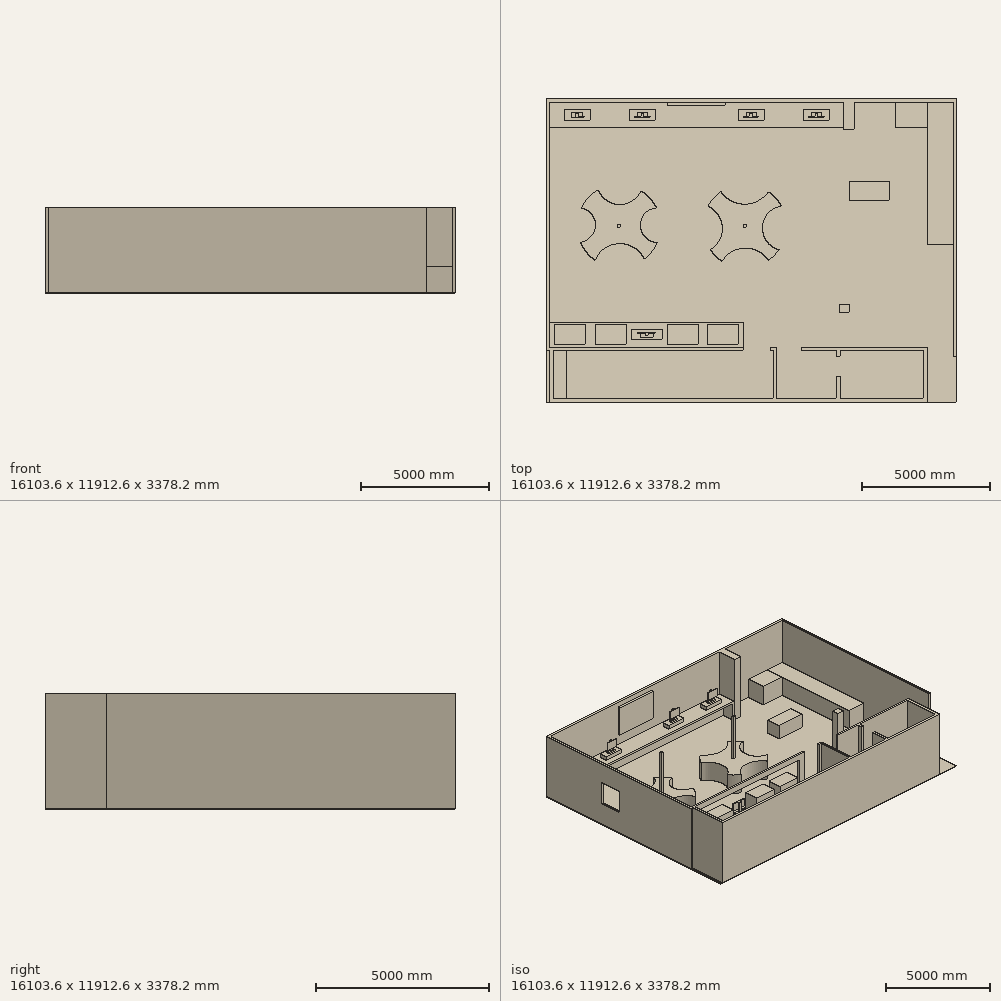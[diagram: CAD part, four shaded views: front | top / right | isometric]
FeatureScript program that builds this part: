
annotation { "Feature Type Name" : "Feature", "Feature Type Description" : "" }
export const myFeature = defineFeature(function(context is Context, id is Id, definition is map)
    precondition{}
    {
        {
            var Q0;
            Q0=qCreatedBy(makeId("Top.planeOp"),FACE);
            var sketch = newSketch(context, id + "F0", { "sketchPlane" : qUnion([Q0])});
            skLineSegment(sketch, "E0", {"start": v(0, 0) * mm, "end": v(0, 4876.8) * mm});
            skLineSegment(sketch, "E1", {"start": v(14833.6, -4876.8) * mm, "end": v(14833.6, -5130.8) * mm});
            skLineSegment(sketch, "E2", {"start": v(15849.6, -5130.8) * mm, "end": v(15849.6, 4876.8) * mm});
            skLineSegment(sketch, "E3", {"start": v(15849.6, 4876.8) * mm, "end": v(11963.4, 4876.8) * mm});
            skLineSegment(sketch, "E4", {"start": v(11963.4, 4876.8) * mm, "end": v(11963.4, 3810) * mm});
            skLineSegment(sketch, "E5", {"start": v(11963.4, 3810) * mm, "end": v(11557, 3810) * mm});
            skLineSegment(sketch, "E6", {"start": v(11557, 3810) * mm, "end": v(11557, 4876.8) * mm});
            skLineSegment(sketch, "E7", {"start": v(11760.2, 1757.31) * mm, "end": v(13335, 1757.31) * mm});
            skPoint(sketch, "E7.startSnap0", {"position": v(11760.2, 3810) * mm});
            skLineSegment(sketch, "E8", {"start": v(13335, 1757.31) * mm, "end": v(13335, 995.31) * mm});
            skLineSegment(sketch, "E9", {"start": v(13335, 995.31) * mm, "end": v(11760.2, 995.31) * mm});
            skLineSegment(sketch, "E10", {"start": v(11760.2, 995.31) * mm, "end": v(11760.2, 1757.31) * mm});
            skLineSegment(sketch, "E11", {"start": v(11760.2, -3062.9) * mm, "end": v(11379.2, -3062.9) * mm});
            skLineSegment(sketch, "E12", {"start": v(11379.2, -3062.9) * mm, "end": v(11379.2, -3393.1) * mm});
            skLineSegment(sketch, "E13", {"start": v(11379.2, -3393.1) * mm, "end": v(11760.2, -3393.1) * mm});
            skLineSegment(sketch, "E14", {"start": v(11760.2, -3393.1) * mm, "end": v(11760.2, -3062.9) * mm});
            skLineSegment(sketch, "E15", {"start": v(0, -4876.8) * mm, "end": v(0, -6908.8) * mm});
            skLineSegment(sketch, "E16", {"start": v(0, -6908.8) * mm, "end": v(8890, -6908.8) * mm});
            skLineSegment(sketch, "E17", {"start": v(8890, -6908.8) * mm, "end": v(14833.6, -6908.8) * mm});
            skLineSegment(sketch, "E18", {"start": v(14833.6, -6908.8) * mm, "end": v(14833.6, -5130.8) * mm});
            skLineSegment(sketch, "E19", {"start": v(11282.33, -4876.8) * mm, "end": v(11282.33, -5130.8) * mm});
            skLineSegment(sketch, "E20", {"start": v(2540, -4876.8) * mm, "end": v(7620, -4876.8) * mm});
            skLineSegment(sketch, "E21", {"start": v(15849.6, -5130.8) * mm, "end": v(15976.6, -5130.8) * mm});
            skLineSegment(sketch, "E22", {"start": v(15976.6, -5130.8) * mm, "end": v(15976.6, 5003.8) * mm});
            skLineSegment(sketch, "E23", {"start": v(15976.6, 5003.8) * mm, "end": v(-127, 5003.8) * mm});
            skLineSegment(sketch, "E24", {"start": v(-127, 5003.8) * mm, "end": v(-127, -4876.8) * mm});
            skLineSegment(sketch, "E25", {"start": v(-127, -4876.8) * mm, "end": v(0, -4876.8) * mm});
            skLineSegment(sketch, "E26", {"start": v(0, 0) * mm, "end": v(0, -4749.8) * mm});
            skLineSegment(sketch, "E27", {"start": v(0, -4749.8) * mm, "end": v(1524, -4749.8) * mm});
            skLineSegment(sketch, "E28", {"start": v(2540, -4749.8) * mm, "end": v(7620, -4749.8) * mm});
            skLineSegment(sketch, "E29", {"start": v(8662.75, -4876.8) * mm, "end": v(8662.75, -4749.8) * mm});
            skLineSegment(sketch, "E30", {"start": v(8662.75, -4749.8) * mm, "end": v(8890, -4749.8) * mm});
            skLineSegment(sketch, "E31", {"start": v(8890, -4749.8) * mm, "end": v(8890, -4876.8) * mm});
            skLineSegment(sketch, "E32", {"start": v(0, 4876.8) * mm, "end": v(11557, 4876.8) * mm});
            skLineSegment(sketch, "E33", {"start": v(8662.75, -4876.8) * mm, "end": v(8789.75, -4876.8) * mm});
            skLineSegment(sketch, "E34", {"start": v(8789.75, -4876.8) * mm, "end": v(8789.75, -6781.8) * mm});
            skLineSegment(sketch, "E35", {"start": v(8789.75, -6781.8) * mm, "end": v(153.75, -6781.8) * mm});
            skLineSegment(sketch, "E36", {"start": v(153.75, -6781.8) * mm, "end": v(153.75, -4876.8) * mm});
            skLineSegment(sketch, "E37", {"start": v(1524, -4876.8) * mm, "end": v(153.75, -4876.8) * mm});
            skLineSegment(sketch, "E38", {"start": v(7620, -4876.8) * mm, "end": v(7620, -4749.8) * mm});
            skLineSegment(sketch, "E39", {"start": v(9906, -4876.8) * mm, "end": v(9906, -4749.8) * mm});
            skLineSegment(sketch, "E40", {"start": v(9906, -4749.8) * mm, "end": v(14833.6, -4749.8) * mm});
            skLineSegment(sketch, "E41", {"start": v(14833.6, -4749.8) * mm, "end": v(14833.6, -4876.8) * mm});
            skLineSegment(sketch, "E42", {"start": v(11282.33, -5130.8) * mm, "end": v(11409.33, -5130.8) * mm});
            skLineSegment(sketch, "E43", {"start": v(11409.33, -5130.8) * mm, "end": v(11409.33, -4876.8) * mm});
            skLineSegment(sketch, "E44", {"start": v(11282.33, -5892.8) * mm, "end": v(11409.33, -5892.8) * mm});
            skLineSegment(sketch, "E45", {"start": v(11409.33, -5892.8) * mm, "end": v(11409.33, -6781.8) * mm});
            skLineSegment(sketch, "E46", {"start": v(9906, -4876.8) * mm, "end": v(11282.33, -4876.8) * mm});
            skLineSegment(sketch, "E47", {"start": v(11409.33, -4876.8) * mm, "end": v(14685.93, -4876.8) * mm});
            skLineSegment(sketch, "E48", {"start": v(14685.93, -4876.8) * mm, "end": v(14685.93, -6781.8) * mm});
            skLineSegment(sketch, "E49", {"start": v(14685.93, -6781.8) * mm, "end": v(11409.33, -6781.8) * mm});
            skLineSegment(sketch, "E50", {"start": v(8890, -4876.8) * mm, "end": v(8890, -6781.8) * mm});
            skLineSegment(sketch, "E51", {"start": v(8890, -6781.8) * mm, "end": v(11282.32, -6781.8) * mm});
            skLineSegment(sketch, "E52", {"start": v(11282.32, -6781.8) * mm, "end": v(11282.33, -5892.8) * mm});
            skLineSegment(sketch, "E53", {"start": v(1524, -4749.8) * mm, "end": v(2540, -4749.8) * mm});
            skLineSegment(sketch, "E54", {"start": v(1524, -4876.8) * mm, "end": v(2540, -4876.8) * mm});
            skSolve(sketch);
        }
        {
            var Q0;
            Q0=makeQuery(id+"F0.imprint","IMPRINT",FACE,{"disambiguationData":[TD([[makeQuery(id+"F0.imprint","IMPRINT",EDGE,{"derivedFrom":sQuery(id+"F0.wireOp",EDGE,"E0")}),1.0]])]});
            var Q1;
            Q1=makeQuery(id+"F0.imprint","IMPRINT",FACE,{"disambiguationData":[TD([[makeQuery(id+"F0.imprint","IMPRINT",EDGE,{"derivedFrom":sQuery(id+"F0.wireOp",EDGE,"E20")}),1.0]])]});
            var Q2;
            Q2=makeQuery(id+"F0.imprint","IMPRINT",FACE,{"disambiguationData":[TD([[makeQuery(id+"F0.imprint","IMPRINT",EDGE,{"derivedFrom":sQuery(id+"F0.wireOp",EDGE,"E11")}),1.0]])]});
            extrude(context, id + "F1", {"entities" : qUnion([Q0, Q1, Q2]), "depth" : 3352.8 * mm, "offsetDistance" : 25.4 * mm});
        }
        {
            var Q0;
            Q0=makeQuery(id+"F0.imprint","IMPRINT",FACE,{"disambiguationData":[TD([[makeQuery(id+"F0.imprint","IMPRINT",EDGE,{"derivedFrom":sQuery(id+"F0.wireOp",EDGE,"E7")}),-1.0]])]});
            extrude(context, id + "F2", {"entities" : qUnion([Q0]), "depth" : 736.6 * mm, "offsetDistance" : 25.4 * mm});
        }
        {
            var Q0;
            Q0=makeQuery(id+"F0.imprint","IMPRINT",FACE,{"disambiguationData":[TD([[makeQuery(id+"F0.imprint","IMPRINT",EDGE,{"derivedFrom":sQuery(id+"F0.wireOp",EDGE,"E0")}),1.0]])]});
            var sketch = newSketch(context, id + "F3", { "sketchPlane" : qUnion([Q0])});
            skLineSegment(sketch, "E55.0", {"start": v(-127, 5003.8) * mm, "end": v(-127, -4876.8) * mm});
            skLineSegment(sketch, "E56.0", {"start": v(0, -6908.8) * mm, "end": v(8890, -6908.8) * mm});
            skLineSegment(sketch, "E57.0", {"start": v(15976.6, 5003.8) * mm, "end": v(-127, 5003.8) * mm});
            skLineSegment(sketch, "E58.0", {"start": v(15976.6, -5130.8) * mm, "end": v(15976.6, 5003.8) * mm});
            skLineSegment(sketch, "E59.bottom", {"start": v(-127, -6908.8) * mm, "end": v(15976.6, -6908.8) * mm});
            skLineSegment(sketch, "E59.top", {"start": v(-127, 5003.8) * mm, "end": v(15976.6, 5003.8) * mm});
            skLineSegment(sketch, "E59.left", {"start": v(-127, -6908.8) * mm, "end": v(-127, 5003.8) * mm});
            skLineSegment(sketch, "E59.right", {"start": v(15976.6, -6908.8) * mm, "end": v(15976.6, 5003.8) * mm});
            skSolve(sketch);
        }
        {
            var Q0;
            Q0 = qSketchRegion(id + "F3", true);
            extrude(context, id + "F4", {"entities" : qUnion([Q0]), "oppositeDirection" : true, "depth" : 25.4 * mm, "offsetDistance" : 25.4 * mm});
        }
        {
            var Q0;
            Q0=makeQuery(id+"F1.opExtrude","SWEPT_FACE",FACE,{"disambiguationData":[OSD([sQuery(id+"F0.wireOp",EDGE,"E0"),sQuery(id+"F0.wireOp",EDGE,"E26")])]});
            var sketch = newSketch(context, id + "F5", { "sketchPlane" : qUnion([Q0])});
            skLineSegment(sketch, "E60", {"start": v(0, 1143) * mm, "end": v(1231.9, 1143) * mm});
            skLineSegment(sketch, "E61", {"start": v(1231.9, 1143) * mm, "end": v(1231.9, 2311.4) * mm});
            skLineSegment(sketch, "E62", {"start": v(1231.9, 2311.4) * mm, "end": v(0, 2311.4) * mm});
            skLineSegment(sketch, "E63", {"start": v(0, 2311.4) * mm, "end": v(0, 1143) * mm});
            skSolve(sketch);
        }
        {
            var Q0;
            Q0 = qSketchRegion(id + "F5", true);
            extrude(context, id + "F6", {"entities" : qUnion([Q0]), "operationType" : NewBodyOperationType.REMOVE, "oppositeDirection" : true, "depth" : 177.8 * mm, "offsetDistance" : 25.4 * mm});
        }
        {
            var Q0;
            Q0=makeQuery(id+"F4.opExtrude","CAP_FACE",FACE,{"disambiguationData":[OSD([sQuery(id+"F3.wireOp",EDGE,"E59.bottom"),sQuery(id+"F3.wireOp",EDGE,"E59.top"),sQuery(id+"F3.wireOp",EDGE,"E59.left"),sQuery(id+"F3.wireOp",EDGE,"E59.right")])],"isStart":true});
            var sketch = newSketch(context, id + "F7", { "sketchPlane" : qUnion([Q0])});
            skCircle(sketch, "E64", {"center": v(2722.99, 0) * mm, "radius": 1638.3 * mm});
            skCircle(sketch, "E65", {"center": v(7663.59, 0) * mm, "radius": 1640.13 * mm});
            skSolve(sketch);
        }
        {
            var Q0;
            Q0=makeQuery(id+"F7.imprint","IMPRINT",FACE,{"disambiguationData":[TD([[makeQuery(id+"F7.imprint","IMPRINT",EDGE,{"derivedFrom":sQuery(id+"F7.wireOp",EDGE,"E64")}),1.0]])]});
            var Q1;
            Q1=makeQuery(id+"F7.imprint","IMPRINT",FACE,{"disambiguationData":[TD([[makeQuery(id+"F7.imprint","IMPRINT",EDGE,{"derivedFrom":sQuery(id+"F7.wireOp",EDGE,"E65")}),1.0]])]});
            extrude(context, id + "F8", {"entities" : qUnion([Q0, Q1]), "operationType" : NewBodyOperationType.ADD, "depth" : 1016 * mm, "offsetDistance" : 25.4 * mm});
        }
        {
            var Q0;
            Q0=makeQuery(id+"F8.opExtrude","CAP_FACE",FACE,{"disambiguationData":[OSD([sQuery(id+"F7.wireOp",EDGE,"E64")])],"isStart":false});
            var sketch = newSketch(context, id + "F9", { "sketchPlane" : qUnion([Q0])});
            skArc(sketch, "E66", {"start": v(1906.26, 1420.2) * mm, "mid": v(2740.7, 849.85) * mm, "end": v(3598.19, 1384.94) * mm});
            skArc(sketch, "E67", {"start": v(1213.38, -636.47) * mm, "mid": v(1800.18, 23.44) * mm, "end": v(1247.63, 712.29) * mm});
            skArc(sketch, "E68", {"start": v(3721.77, -1298.64) * mm, "mid": v(2740.3, -685.3) * mm, "end": v(1791.02, -1347.4) * mm});
            skArc(sketch, "E69", {"start": v(4198.34, 712.29) * mm, "mid": v(3564.92, 21.38) * mm, "end": v(4232.6, -636.47) * mm});
            skSolve(sketch);
        }
        {
            var Q0;
            {var subQ0=sQuery(id+"F9.wireOp",EDGE,"E66");Q0=makeQuery(id+"F9.imprint","IMPRINT",FACE,{"disambiguationData":[TD([[makeQuery(id+"F9.imprint","IMPRINT",EDGE,{"derivedFrom":subQ0}),1.0]])]});}
            var Q1;
            {var subQ0=sQuery(id+"F9.wireOp",EDGE,"E67");Q1=makeQuery(id+"F9.imprint","IMPRINT",FACE,{"disambiguationData":[TD([[makeQuery(id+"F9.imprint","IMPRINT",EDGE,{"derivedFrom":subQ0}),1.0]])]});}
            var Q2;
            {var subQ0=sQuery(id+"F9.wireOp",EDGE,"E68");Q2=makeQuery(id+"F9.imprint","IMPRINT",FACE,{"disambiguationData":[TD([[makeQuery(id+"F9.imprint","IMPRINT",EDGE,{"derivedFrom":subQ0}),1.0]])]});}
            var Q3;
            {var subQ0=sQuery(id+"F9.wireOp",EDGE,"E69");Q3=makeQuery(id+"F9.imprint","IMPRINT",FACE,{"disambiguationData":[TD([[makeQuery(id+"F9.imprint","IMPRINT",EDGE,{"derivedFrom":subQ0}),1.0]])]});}
            var Q4;
            Q4=makeQuery(id+"F4.opExtrude","CAP_FACE",FACE,{"disambiguationData":[OSD([sQuery(id+"F3.wireOp",EDGE,"E59.bottom"),sQuery(id+"F3.wireOp",EDGE,"E59.top"),sQuery(id+"F3.wireOp",EDGE,"E59.left"),sQuery(id+"F3.wireOp",EDGE,"E59.right")])],"isStart":true});
            extrude(context, id + "F10", {"entities" : qUnion([Q0, Q1, Q2, Q3]), "operationType" : NewBodyOperationType.REMOVE, "endBound" : BoundingType.UP_TO_SURFACE, "oppositeDirection" : true, "depth" : 25.4 * mm, "endBoundEntityFace" : qUnion([Q4]), "offsetDistance" : 25.4 * mm});
        }
        {
            var Q0;
            Q0=makeQuery(id+"F8.opExtrude","CAP_FACE",FACE,{"disambiguationData":[OSD([sQuery(id+"F7.wireOp",EDGE,"E65")])],"isStart":false});
            var sketch = newSketch(context, id + "F11", { "sketchPlane" : qUnion([Q0])});
            skArc(sketch, "E70", {"start": v(6726.29, 1345.91) * mm, "mid": v(7662.51, 863.3) * mm, "end": v(8597.53, 1348.25) * mm});
            skArc(sketch, "E71", {"start": v(6311.2, -927.92) * mm, "mid": v(6782.4, -46.3) * mm, "end": v(6221.4, 781.08) * mm});
            skArc(sketch, "E72", {"start": v(8597.53, -1348.25) * mm, "mid": v(7680.2, -859.78) * mm, "end": v(6782.4, -1383.3) * mm});
            skPoint(sketch, "E72.endSnap0", {"position": v(6782.4, -46.3) * mm});
            skArc(sketch, "E73", {"start": v(9105.79, 781.08) * mm, "mid": v(8358, -36.49) * mm, "end": v(9015.99, -927.92) * mm});
            skSolve(sketch);
        }
        {
            var Q0;
            {var subQ0=sQuery(id+"F11.wireOp",EDGE,"E70");Q0=makeQuery(id+"F11.imprint","IMPRINT",FACE,{"disambiguationData":[TD([[makeQuery(id+"F11.imprint","IMPRINT",EDGE,{"derivedFrom":subQ0}),1.0]])]});}
            var Q1;
            {var subQ0=sQuery(id+"F11.wireOp",EDGE,"E71");Q1=makeQuery(id+"F11.imprint","IMPRINT",FACE,{"disambiguationData":[TD([[makeQuery(id+"F11.imprint","IMPRINT",EDGE,{"derivedFrom":subQ0}),1.0]])]});}
            var Q2;
            {var subQ0=sQuery(id+"F11.wireOp",EDGE,"E72");Q2=makeQuery(id+"F11.imprint","IMPRINT",FACE,{"disambiguationData":[TD([[makeQuery(id+"F11.imprint","IMPRINT",EDGE,{"derivedFrom":subQ0}),1.0]])]});}
            var Q3;
            {var subQ0=sQuery(id+"F11.wireOp",EDGE,"E73");Q3=makeQuery(id+"F11.imprint","IMPRINT",FACE,{"disambiguationData":[TD([[makeQuery(id+"F11.imprint","IMPRINT",EDGE,{"derivedFrom":subQ0}),1.0]])]});}
            var Q4;
            {var subQ0=sQuery(id+"F3.wireOp",EDGE,"E59.right");var subQ1=sQuery(id+"F3.wireOp",EDGE,"E59.left");var subQ2=sQuery(id+"F3.wireOp",EDGE,"E59.top");var subQ3=sQuery(id+"F3.wireOp",EDGE,"E59.bottom");Q4=makeQuery(id+"F10.boolean.opBoolean","MERGE",FACE,{"derivedFrom":[makeQuery(id+"F4.opExtrude","CAP_FACE",FACE,{"disambiguationData":[OSD([subQ3,subQ2,subQ1,subQ0])],"isStart":true}),makeQuery(id+"F10.opExtrude","CAP_FACE",FACE,{"disambiguationData":[OSD([subQ3,subQ2,subQ1,subQ0]),OD(0.0)],"isStart":false}),makeQuery(id+"F10.opExtrude","CAP_FACE",FACE,{"disambiguationData":[OSD([subQ3,subQ2,subQ1,subQ0]),OD(1.0)],"isStart":false}),makeQuery(id+"F10.opExtrude","CAP_FACE",FACE,{"disambiguationData":[OSD([subQ3,subQ2,subQ1,subQ0]),OD(2.0)],"isStart":false}),makeQuery(id+"F10.opExtrude","CAP_FACE",FACE,{"disambiguationData":[OSD([subQ3,subQ2,subQ1,subQ0]),OD(3.0)],"isStart":false})]});}
            extrude(context, id + "F12", {"entities" : qUnion([Q0, Q1, Q2, Q3]), "operationType" : NewBodyOperationType.REMOVE, "endBound" : BoundingType.UP_TO_SURFACE, "oppositeDirection" : true, "depth" : 25.4 * mm, "endBoundEntityFace" : qUnion([Q4]), "offsetDistance" : 25.4 * mm});
        }
        {
            var Q0;
            {var subQ0=sQuery(id+"F3.wireOp",EDGE,"E59.right");var subQ1=sQuery(id+"F3.wireOp",EDGE,"E59.left");var subQ2=sQuery(id+"F3.wireOp",EDGE,"E59.top");var subQ3=sQuery(id+"F3.wireOp",EDGE,"E59.bottom");Q0=makeQuery(id+"F12.boolean.opBoolean","MERGE",FACE,{"derivedFrom":[makeQuery(id+"F10.boolean.opBoolean","MERGE",FACE,{"derivedFrom":[makeQuery(id+"F4.opExtrude","CAP_FACE",FACE,{"disambiguationData":[OSD([subQ3,subQ2,subQ1,subQ0])],"isStart":true}),makeQuery(id+"F10.opExtrude","CAP_FACE",FACE,{"disambiguationData":[OSD([subQ3,subQ2,subQ1,subQ0]),OD(0.0)],"isStart":false}),makeQuery(id+"F10.opExtrude","CAP_FACE",FACE,{"disambiguationData":[OSD([subQ3,subQ2,subQ1,subQ0]),OD(1.0)],"isStart":false}),makeQuery(id+"F10.opExtrude","CAP_FACE",FACE,{"disambiguationData":[OSD([subQ3,subQ2,subQ1,subQ0]),OD(2.0)],"isStart":false}),makeQuery(id+"F10.opExtrude","CAP_FACE",FACE,{"disambiguationData":[OSD([subQ3,subQ2,subQ1,subQ0]),OD(3.0)],"isStart":false})]}),makeQuery(id+"F12.opExtrude","CAP_FACE",FACE,{"disambiguationData":[OSD([subQ3,subQ2,subQ1,subQ0]),OD(0.0)],"isStart":false}),makeQuery(id+"F12.opExtrude","CAP_FACE",FACE,{"disambiguationData":[OSD([subQ3,subQ2,subQ1,subQ0]),OD(1.0)],"isStart":false}),makeQuery(id+"F12.opExtrude","CAP_FACE",FACE,{"disambiguationData":[OSD([subQ3,subQ2,subQ1,subQ0]),OD(2.0)],"isStart":false}),makeQuery(id+"F12.opExtrude","CAP_FACE",FACE,{"disambiguationData":[OSD([subQ3,subQ2,subQ1,subQ0]),OD(3.0)],"isStart":false})]});}
            var sketch = newSketch(context, id + "F13", { "sketchPlane" : qUnion([Q0])});
            skPoint(sketch, "E74.0", {"position": v(0, -4749.8) * mm});
            skPoint(sketch, "E75.0", {"position": v(7620, -4749.8) * mm});
            skLineSegment(sketch, "E76.bottom", {"start": v(7620, -4749.8) * mm, "end": v(0, -4749.8) * mm});
            skLineSegment(sketch, "E76.top", {"start": v(7620, -3769.1) * mm, "end": v(0, -3769.1) * mm});
            skLineSegment(sketch, "E76.left", {"start": v(7620, -4749.8) * mm, "end": v(7620, -3769.1) * mm});
            skLineSegment(sketch, "E76.right", {"start": v(0, -4749.8) * mm, "end": v(0, -3769.1) * mm});
            skSolve(sketch);
        }
        {
            var Q0;
            Q0=makeQuery(id+"F13.imprint","IMPRINT",FACE,{"disambiguationData":[TD([[makeQuery(id+"F13.imprint","IMPRINT",EDGE,{"derivedFrom":sQuery(id+"F13.wireOp",EDGE,"E76.bottom")}),-1.0]])]});
            extrude(context, id + "F14", {"entities" : qUnion([Q0]), "depth" : 1016 * mm, "offsetDistance" : 25.4 * mm});
        }
        {
            var Q0;
            Q0=makeQuery(id+"F1.opExtrude","SWEPT_FACE",FACE,{"disambiguationData":[OSD([sQuery(id+"F0.wireOp",EDGE,"E27"),sQuery(id+"F0.wireOp",EDGE,"E28"),sQuery(id+"F0.wireOp",EDGE,"E53")])]});
            var sketch = newSketch(context, id + "F15", { "sketchPlane" : qUnion([Q0])});
            skLineSegment(sketch, "E77.bottom", {"start": v(-7283.7, 3047.44) * mm, "end": v(-328.54, 3047.44) * mm});
            skLineSegment(sketch, "E77.top", {"start": v(-7283.7, 1431.93) * mm, "end": v(-328.54, 1431.93) * mm});
            skLineSegment(sketch, "E77.left", {"start": v(-7283.7, 3047.44) * mm, "end": v(-7283.7, 1431.93) * mm});
            skLineSegment(sketch, "E77.right", {"start": v(-328.54, 3047.44) * mm, "end": v(-328.54, 1431.93) * mm});
            skSolve(sketch);
        }
        {
            var Q0;
            Q0=makeQuery(id+"F15.imprint","IMPRINT",FACE,{"disambiguationData":[TD([[makeQuery(id+"F15.imprint","IMPRINT",EDGE,{"derivedFrom":sQuery(id+"F15.wireOp",EDGE,"E77.bottom")}),-1.0]])]});
            extrude(context, id + "F16", {"entities" : qUnion([Q0]), "operationType" : NewBodyOperationType.REMOVE, "endBound" : BoundingType.UP_TO_NEXT, "oppositeDirection" : true, "depth" : 25.4 * mm, "offsetDistance" : 25.4 * mm});
        }
        {
            var Q0;
            Q0=makeQuery(id+"F1.opExtrude","SWEPT_FACE",FACE,{"disambiguationData":[OSD([sQuery(id+"F0.wireOp",EDGE,"E32")])]});
            var sketch = newSketch(context, id + "F17", { "sketchPlane" : qUnion([Q0])});
            skLineSegment(sketch, "E78", {"start": v(0, 0) * mm, "end": v(11557, 0) * mm});
            skLineSegment(sketch, "E79", {"start": v(11557, 0) * mm, "end": v(11557, 1016) * mm});
            skLineSegment(sketch, "E80.0", {"start": v(0, 3352.8) * mm, "end": v(0, 0) * mm});
            skLineSegment(sketch, "E81", {"start": v(11557, 1016) * mm, "end": v(0, 1016) * mm});
            skLineSegment(sketch, "E82", {"start": v(0, 1016) * mm, "end": v(0, 0) * mm});
            skSolve(sketch);
        }
        {
            var Q0;
            Q0=makeQuery(id+"F17.imprint","IMPRINT",FACE,{"disambiguationData":[TD([[makeQuery(id+"F17.imprint","IMPRINT",EDGE,{"derivedFrom":sQuery(id+"F17.wireOp",EDGE,"E78")}),1.0]])]});
            extrude(context, id + "F18", {"entities" : qUnion([Q0]), "depth" : 1016 * mm, "offsetDistance" : 25.4 * mm});
        }
        {
            var Q0;
            Q0=makeQuery(id+"F18.opExtrude","CAP_FACE",FACE,{"disambiguationData":[OSD([sQuery(id+"F17.wireOp",EDGE,"E78"),sQuery(id+"F17.wireOp",EDGE,"E79"),sQuery(id+"F17.wireOp",EDGE,"E81"),sQuery(id+"F17.wireOp",EDGE,"E82")])],"isStart":false});
            var sketch = newSketch(context, id + "F19", { "sketchPlane" : qUnion([Q0])});
            skLineSegment(sketch, "E83.bottom", {"start": v(101.6, 0) * mm, "end": v(11455.4, 0) * mm});
            skLineSegment(sketch, "E83.top", {"start": v(101.6, 914.4) * mm, "end": v(11455.4, 914.4) * mm});
            skLineSegment(sketch, "E83.left", {"start": v(101.6, 0) * mm, "end": v(101.6, 914.4) * mm});
            skLineSegment(sketch, "E83.right", {"start": v(11455.4, 0) * mm, "end": v(11455.4, 914.4) * mm});
            skSolve(sketch);
        }
        {
            var Q0;
            Q0 = qSketchRegion(id + "F19", true);
            extrude(context, id + "F20", {"entities" : qUnion([Q0]), "operationType" : NewBodyOperationType.REMOVE, "oppositeDirection" : true, "depth" : 635 * mm, "offsetDistance" : 25.4 * mm});
        }
        {
            var Q0;
            Q0=makeQuery(id+"F1.opExtrude","SWEPT_FACE",FACE,{"disambiguationData":[OSD([sQuery(id+"F0.wireOp",EDGE,"E36")])]});
            var sketch = newSketch(context, id + "F21", { "sketchPlane" : qUnion([Q0])});
            skLineSegment(sketch, "E84", {"start": v(-6781.8, 0) * mm, "end": v(-6781.8, 1905) * mm});
            skLineSegment(sketch, "E85", {"start": v(-6781.8, 1905) * mm, "end": v(-4876.8, 1905) * mm});
            skLineSegment(sketch, "E86", {"start": v(-4876.8, 1905) * mm, "end": v(-4876.8, 0) * mm});
            skLineSegment(sketch, "E87", {"start": v(-4876.8, 0) * mm, "end": v(-6781.8, 0) * mm});
            skSolve(sketch);
        }
        {
            var Q0;
            Q0 = qSketchRegion(id + "F21", true);
            extrude(context, id + "F22", {"entities" : qUnion([Q0]), "depth" : 508 * mm, "offsetDistance" : 25.4 * mm});
        }
        {
            var Q0;
            Q0=makeQuery(id+"F1.opExtrude","SWEPT_FACE",FACE,{"disambiguationData":[OSD([sQuery(id+"F0.wireOp",EDGE,"E2")])]});
            var sketch = newSketch(context, id + "F23", { "sketchPlane" : qUnion([Q0])});
            skLineSegment(sketch, "E88", {"start": v(-4876.8, 0) * mm, "end": v(-4876.8, 1016) * mm});
            skLineSegment(sketch, "E89", {"start": v(-4876.8, 1016) * mm, "end": v(711.2, 1016) * mm});
            skLineSegment(sketch, "E90", {"start": v(711.2, 1016) * mm, "end": v(711.2, 0) * mm});
            skLineSegment(sketch, "E91", {"start": v(711.2, 0) * mm, "end": v(-4876.8, 0) * mm});
            skSolve(sketch);
        }
        {
            var Q0;
            Q0 = qSketchRegion(id + "F23", true);
            extrude(context, id + "F24", {"entities" : qUnion([Q0]), "depth" : 1016 * mm, "offsetDistance" : 25.4 * mm});
        }
        {
            var Q0;
            Q0=makeQuery(id+"F24.opExtrude","CAP_FACE",FACE,{"disambiguationData":[OSD([sQuery(id+"F23.wireOp",EDGE,"E88"),sQuery(id+"F23.wireOp",EDGE,"E89"),sQuery(id+"F23.wireOp",EDGE,"E90"),sQuery(id+"F23.wireOp",EDGE,"E91")])],"isStart":false});
            var sketch = newSketch(context, id + "F25", { "sketchPlane" : qUnion([Q0])});
            skLineSegment(sketch, "E92", {"start": v(-4876.8, 0) * mm, "end": v(-4876.8, 1016) * mm});
            skLineSegment(sketch, "E93", {"start": v(-4876.8, 1016) * mm, "end": v(-3860.8, 1016) * mm});
            skLineSegment(sketch, "E94", {"start": v(-3860.8, 1016) * mm, "end": v(-3860.8, 0) * mm});
            skLineSegment(sketch, "E95", {"start": v(-3860.8, 0) * mm, "end": v(-4876.8, 0) * mm});
            skSolve(sketch);
        }
        {
            var Q0;
            Q0 = qSketchRegion(id + "F25", true);
            extrude(context, id + "F26", {"entities" : qUnion([Q0]), "depth" : 1270 * mm, "offsetDistance" : 25.4 * mm});
        }
        {
            var Q0;
            Q0=makeQuery(id+"F18.opExtrude","SWEPT_FACE",FACE,{"disambiguationData":[OSD([sQuery(id+"F17.wireOp",EDGE,"E81")])]});
            var sketch = newSketch(context, id + "F27", { "sketchPlane" : qUnion([Q0])});
            skLineSegment(sketch, "E96.0.0", {"start": v(11557, 4876.8) * mm, "end": v(0, 4876.8) * mm});
            skLineSegment(sketch, "E96.0.1", {"start": v(0, 4876.8) * mm, "end": v(0, 3860.8) * mm});
            skLineSegment(sketch, "E96.0.2", {"start": v(0, 3860.8) * mm, "end": v(11557, 3860.8) * mm});
            skLineSegment(sketch, "E96.0.3", {"start": v(11557, 3860.8) * mm, "end": v(11557, 4876.8) * mm});
            skLineSegment(sketch, "E97", {"start": v(566.49, 4368.8) * mm, "end": v(566.49, 4165.6) * mm});
            skPoint(sketch, "E97.startSnap0", {"position": v(0, 4368.8) * mm});
            skLineSegment(sketch, "E98", {"start": v(566.49, 4165.6) * mm, "end": v(1582.49, 4165.6) * mm});
            skLineSegment(sketch, "E99", {"start": v(1582.49, 4165.6) * mm, "end": v(1582.49, 4572) * mm});
            skLineSegment(sketch, "E100", {"start": v(1582.49, 4572) * mm, "end": v(566.49, 4572) * mm});
            skLineSegment(sketch, "E101", {"start": v(566.49, 4572) * mm, "end": v(566.49, 4368.8) * mm});
            skLineSegment(sketch, "E102", {"start": v(2358.83, 4876.8) * mm, "end": v(2358.83, 3860.8) * mm});
            skLineSegment(sketch, "E103.MirrorCS", {"start": v(3135.17, 4165.6) * mm, "end": v(3135.17, 4572) * mm});
            skLineSegment(sketch, "E104.MirrorCS", {"start": v(4151.17, 4165.6) * mm, "end": v(3135.17, 4165.6) * mm});
            skLineSegment(sketch, "E105.MirrorCS", {"start": v(3135.17, 4572) * mm, "end": v(4151.17, 4572) * mm});
            skLineSegment(sketch, "E106.MirrorCS", {"start": v(4151.17, 4368.8) * mm, "end": v(4151.17, 4165.6) * mm});
            skLineSegment(sketch, "E107.MirrorCS", {"start": v(4151.17, 4572) * mm, "end": v(4151.17, 4368.8) * mm});
            skLineSegment(sketch, "E108", {"start": v(5778.5, 3860.8) * mm, "end": v(5778.5, 4876.8) * mm});
            skLineSegment(sketch, "E109.MirrorCS", {"start": v(7405.83, 4165.6) * mm, "end": v(8421.83, 4165.6) * mm});
            skLineSegment(sketch, "E110.MirrorCS", {"start": v(8421.83, 4572) * mm, "end": v(7405.83, 4572) * mm});
            skLineSegment(sketch, "E111.MirrorCS", {"start": v(8421.83, 4165.6) * mm, "end": v(8421.83, 4572) * mm});
            skLineSegment(sketch, "E112.MirrorCS", {"start": v(7405.83, 4368.8) * mm, "end": v(7405.83, 4165.6) * mm});
            skLineSegment(sketch, "E113.MirrorCS", {"start": v(7405.83, 4572) * mm, "end": v(7405.83, 4368.8) * mm});
            skLineSegment(sketch, "E114.MirrorCS", {"start": v(10990.51, 4368.8) * mm, "end": v(10990.51, 4165.6) * mm});
            skLineSegment(sketch, "E115.MirrorCS", {"start": v(10990.51, 4572) * mm, "end": v(10990.51, 4368.8) * mm});
            skLineSegment(sketch, "E116.MirrorCS", {"start": v(9974.51, 4572) * mm, "end": v(10990.51, 4572) * mm});
            skLineSegment(sketch, "E117.MirrorCS", {"start": v(9974.51, 4165.6) * mm, "end": v(9974.51, 4572) * mm});
            skLineSegment(sketch, "E118.MirrorCS", {"start": v(10990.51, 4165.6) * mm, "end": v(9974.51, 4165.6) * mm});
            skSolve(sketch);
        }
        {
            var Q0;
            Q0=makeQuery(id+"F27.imprint","IMPRINT",FACE,{"disambiguationData":[TD([[makeQuery(id+"F27.imprint","IMPRINT",EDGE,{"derivedFrom":sQuery(id+"F27.wireOp",EDGE,"E97")}),1.0]])]});
            var Q1;
            Q1=makeQuery(id+"F27.imprint","IMPRINT",FACE,{"disambiguationData":[TD([[makeQuery(id+"F27.imprint","IMPRINT",EDGE,{"derivedFrom":sQuery(id+"F27.wireOp",EDGE,"E103.MirrorCS")}),-1.0]])]});
            var Q2;
            Q2=makeQuery(id+"F27.imprint","IMPRINT",FACE,{"disambiguationData":[TD([[makeQuery(id+"F27.imprint","IMPRINT",EDGE,{"derivedFrom":sQuery(id+"F27.wireOp",EDGE,"E109.MirrorCS")}),1.0]])]});
            var Q3;
            Q3=makeQuery(id+"F27.imprint","IMPRINT",FACE,{"disambiguationData":[TD([[makeQuery(id+"F27.imprint","IMPRINT",EDGE,{"derivedFrom":sQuery(id+"F27.wireOp",EDGE,"E114.MirrorCS")}),-1.0]])]});
            extrude(context, id + "F28", {"entities" : qUnion([Q0, Q1, Q2, Q3]), "operationType" : NewBodyOperationType.ADD, "depth" : 203.2 * mm, "offsetDistance" : 25.4 * mm});
        }
        {
            var Q0;
            Q0=makeQuery(id+"F28.opExtrude","CAP_FACE",FACE,{"disambiguationData":[OSD([sQuery(id+"F27.wireOp",EDGE,"E97"),sQuery(id+"F27.wireOp",EDGE,"E98"),sQuery(id+"F27.wireOp",EDGE,"E99"),sQuery(id+"F27.wireOp",EDGE,"E100"),sQuery(id+"F27.wireOp",EDGE,"E101")])],"isStart":false});
            var sketch = newSketch(context, id + "F29", { "sketchPlane" : qUnion([Q0])});
            skPoint(sketch, "E119.startSnap0", {"position": v(566.49, 4368.8) * mm});
            skPoint(sketch, "E119.startSnap1", {"position": v(1074.49, 4572) * mm});
            skLineSegment(sketch, "E120", {"start": v(871.29, 4368.8) * mm, "end": v(871.29, 4267.2) * mm});
            skLineSegment(sketch, "E121", {"start": v(871.29, 4267.2) * mm, "end": v(1277.69, 4267.2) * mm});
            skLineSegment(sketch, "E122", {"start": v(1277.69, 4267.2) * mm, "end": v(1277.69, 4470.4) * mm});
            skLineSegment(sketch, "E123", {"start": v(1277.69, 4470.4) * mm, "end": v(871.29, 4470.4) * mm});
            skLineSegment(sketch, "E124", {"start": v(871.29, 4470.4) * mm, "end": v(871.29, 4368.8) * mm});
            skLineSegment(sketch, "E125.0", {"start": v(11557, 3860.8) * mm, "end": v(0, 3860.8) * mm});
            skLineSegment(sketch, "E126.0.0", {"start": v(11557, 4876.8) * mm, "end": v(0, 4876.8) * mm});
            skLineSegment(sketch, "E126.0.1", {"start": v(0, 4876.8) * mm, "end": v(0, 3860.8) * mm});
            skLineSegment(sketch, "E126.0.2", {"start": v(0, 3860.8) * mm, "end": v(11557, 3860.8) * mm});
            skLineSegment(sketch, "E126.0.3", {"start": v(11557, 3860.8) * mm, "end": v(11557, 4876.8) * mm});
            skLineSegment(sketch, "E127.0.0", {"start": v(4151.17, 4165.6) * mm, "end": v(4151.17, 4572) * mm});
            skLineSegment(sketch, "E127.0.1", {"start": v(4151.17, 4572) * mm, "end": v(3135.17, 4572) * mm});
            skLineSegment(sketch, "E127.0.2", {"start": v(3135.17, 4572) * mm, "end": v(3135.17, 4165.6) * mm});
            skLineSegment(sketch, "E127.0.3", {"start": v(3135.17, 4165.6) * mm, "end": v(4151.17, 4165.6) * mm});
            skLineSegment(sketch, "E128", {"start": v(2358.83, 3860.8) * mm, "end": v(2358.83, 4876.8) * mm});
            skLineSegment(sketch, "E129.MirrorCS", {"start": v(3846.37, 4267.2) * mm, "end": v(3439.97, 4267.2) * mm});
            skLineSegment(sketch, "E130.MirrorCS", {"start": v(3846.37, 4368.8) * mm, "end": v(3846.37, 4267.2) * mm});
            skLineSegment(sketch, "E131.MirrorCS", {"start": v(3846.37, 4470.4) * mm, "end": v(3846.37, 4368.8) * mm});
            skLineSegment(sketch, "E132.MirrorCS", {"start": v(3439.97, 4470.4) * mm, "end": v(3846.37, 4470.4) * mm});
            skLineSegment(sketch, "E133.MirrorCS", {"start": v(3439.97, 4267.2) * mm, "end": v(3439.97, 4470.4) * mm});
            skLineSegment(sketch, "E134", {"start": v(5778.5, 3860.8) * mm, "end": v(5778.5, 4876.8) * mm});
            skLineSegment(sketch, "E135.MirrorCS", {"start": v(7710.63, 4267.2) * mm, "end": v(8117.03, 4267.2) * mm});
            skLineSegment(sketch, "E136.MirrorCS", {"start": v(8117.03, 4267.2) * mm, "end": v(8117.03, 4470.4) * mm});
            skLineSegment(sketch, "E137.MirrorCS", {"start": v(8117.03, 4470.4) * mm, "end": v(7710.63, 4470.4) * mm});
            skLineSegment(sketch, "E138.MirrorCS", {"start": v(7710.63, 4470.4) * mm, "end": v(7710.63, 4368.8) * mm});
            skLineSegment(sketch, "E139.MirrorCS", {"start": v(7710.63, 4368.8) * mm, "end": v(7710.63, 4267.2) * mm});
            skLineSegment(sketch, "E140.MirrorCS", {"start": v(10685.71, 4267.2) * mm, "end": v(10279.31, 4267.2) * mm});
            skLineSegment(sketch, "E141.MirrorCS", {"start": v(10279.31, 4470.4) * mm, "end": v(10685.71, 4470.4) * mm});
            skLineSegment(sketch, "E142.MirrorCS", {"start": v(10685.71, 4470.4) * mm, "end": v(10685.71, 4368.8) * mm});
            skLineSegment(sketch, "E143.MirrorCS", {"start": v(10685.71, 4368.8) * mm, "end": v(10685.71, 4267.2) * mm});
            skLineSegment(sketch, "E144.MirrorCS", {"start": v(10279.31, 4267.2) * mm, "end": v(10279.31, 4470.4) * mm});
            skSolve(sketch);
        }
        {
            var Q0;
            Q0=makeQuery(id+"F29.imprint","IMPRINT",FACE,{"disambiguationData":[TD([[makeQuery(id+"F29.imprint","IMPRINT",EDGE,{"derivedFrom":sQuery(id+"F29.wireOp",EDGE,"E120")}),1.0]])]});
            var Q1;
            Q1=makeQuery(id+"F29.imprint","IMPRINT",FACE,{"disambiguationData":[TD([[makeQuery(id+"F29.imprint","IMPRINT",EDGE,{"derivedFrom":sQuery(id+"F29.wireOp",EDGE,"E129.MirrorCS")}),-1.0]])]});
            var Q2;
            Q2=makeQuery(id+"F29.imprint","IMPRINT",FACE,{"disambiguationData":[TD([[makeQuery(id+"F29.imprint","IMPRINT",EDGE,{"derivedFrom":sQuery(id+"F29.wireOp",EDGE,"E135.MirrorCS")}),1.0]])]});
            var Q3;
            Q3=makeQuery(id+"F29.imprint","IMPRINT",FACE,{"disambiguationData":[TD([[makeQuery(id+"F29.imprint","IMPRINT",EDGE,{"derivedFrom":sQuery(id+"F29.wireOp",EDGE,"E140.MirrorCS")}),-1.0]])]});
            extrude(context, id + "F30", {"entities" : qUnion([Q0, Q1, Q2, Q3]), "operationType" : NewBodyOperationType.ADD, "depth" : 76.2 * mm, "offsetDistance" : 25.4 * mm});
        }
        {
            var Q0;
            Q0=makeQuery(id+"F30.opExtrude","CAP_FACE",FACE,{"disambiguationData":[OSD([sQuery(id+"F29.wireOp",EDGE,"E120"),sQuery(id+"F29.wireOp",EDGE,"E121"),sQuery(id+"F29.wireOp",EDGE,"E122"),sQuery(id+"F29.wireOp",EDGE,"E123"),sQuery(id+"F29.wireOp",EDGE,"E124")])],"isStart":false});
            var sketch = newSketch(context, id + "F31", { "sketchPlane" : qUnion([Q0])});
            skPoint(sketch, "E145.startSnap0", {"position": v(871.29, 4368.8) * mm});
            skPoint(sketch, "E145.startSnap1", {"position": v(1074.49, 4267.2) * mm});
            skLineSegment(sketch, "E146", {"start": v(1074.49, 4419.6) * mm, "end": v(1023.69, 4419.6) * mm});
            skLineSegment(sketch, "E147", {"start": v(1023.69, 4419.6) * mm, "end": v(1023.69, 4318) * mm});
            skLineSegment(sketch, "E148", {"start": v(1023.69, 4318) * mm, "end": v(1125.29, 4318) * mm});
            skLineSegment(sketch, "E149", {"start": v(1125.29, 4318) * mm, "end": v(1125.29, 4419.6) * mm});
            skLineSegment(sketch, "E150", {"start": v(1125.29, 4419.6) * mm, "end": v(1074.49, 4419.6) * mm});
            skLineSegment(sketch, "E151.0.0", {"start": v(11557, 4876.8) * mm, "end": v(0, 4876.8) * mm});
            skLineSegment(sketch, "E151.0.1", {"start": v(0, 4876.8) * mm, "end": v(0, 3860.8) * mm});
            skLineSegment(sketch, "E151.0.2", {"start": v(0, 3860.8) * mm, "end": v(11557, 3860.8) * mm});
            skLineSegment(sketch, "E151.0.3", {"start": v(11557, 3860.8) * mm, "end": v(11557, 4876.8) * mm});
            skLineSegment(sketch, "E152.MirrorCS", {"start": v(10533.31, 4419.6) * mm, "end": v(10533.31, 4318) * mm});
            skLineSegment(sketch, "E153.MirrorCS", {"start": v(10431.71, 4419.6) * mm, "end": v(10482.51, 4419.6) * mm});
            skLineSegment(sketch, "E154.MirrorCS", {"start": v(10482.51, 4419.6) * mm, "end": v(10533.31, 4419.6) * mm});
            skLineSegment(sketch, "E155.MirrorCS", {"start": v(10533.31, 4318) * mm, "end": v(10431.71, 4318) * mm});
            skLineSegment(sketch, "E156", {"start": v(10431.71, 4318) * mm, "end": v(10431.71, 4419.6) * mm});
            skLineSegment(sketch, "E157.0.0", {"start": v(4151.17, 4165.6) * mm, "end": v(4151.17, 4572) * mm});
            skLineSegment(sketch, "E157.0.1", {"start": v(4151.17, 4572) * mm, "end": v(3135.17, 4572) * mm});
            skLineSegment(sketch, "E157.0.2", {"start": v(3135.17, 4572) * mm, "end": v(3135.17, 4165.6) * mm});
            skLineSegment(sketch, "E157.0.3", {"start": v(3135.17, 4165.6) * mm, "end": v(4151.17, 4165.6) * mm});
            skLineSegment(sketch, "E158.MirrorCS", {"start": v(3693.97, 4419.6) * mm, "end": v(3693.97, 4318) * mm});
            skLineSegment(sketch, "E159.MirrorCS", {"start": v(3643.17, 4419.6) * mm, "end": v(3693.97, 4419.6) * mm});
            skLineSegment(sketch, "E160.MirrorCS", {"start": v(3592.37, 4419.6) * mm, "end": v(3643.17, 4419.6) * mm});
            skLineSegment(sketch, "E161.MirrorCS", {"start": v(3693.97, 4318) * mm, "end": v(3592.37, 4318) * mm});
            skLineSegment(sketch, "E162", {"start": v(3592.37, 4318) * mm, "end": v(3592.37, 4419.6) * mm});
            skLineSegment(sketch, "E163", {"start": v(5778.5, 3860.8) * mm, "end": v(5778.5, 4876.8) * mm});
            skLineSegment(sketch, "E164.MirrorCS", {"start": v(7863.03, 4318) * mm, "end": v(7964.63, 4318) * mm});
            skLineSegment(sketch, "E165.MirrorCS", {"start": v(7964.63, 4318) * mm, "end": v(7964.63, 4419.6) * mm});
            skLineSegment(sketch, "E166.MirrorCS", {"start": v(7863.03, 4419.6) * mm, "end": v(7863.03, 4318) * mm});
            skLineSegment(sketch, "E167.MirrorCS", {"start": v(7913.83, 4419.6) * mm, "end": v(7863.03, 4419.6) * mm});
            skLineSegment(sketch, "E168.MirrorCS", {"start": v(7964.63, 4419.6) * mm, "end": v(7913.83, 4419.6) * mm});
            skSolve(sketch);
        }
        {
            var Q0;
            Q0=makeQuery(id+"F31.imprint","IMPRINT",FACE,{"disambiguationData":[TD([[makeQuery(id+"F31.imprint","IMPRINT",EDGE,{"derivedFrom":sQuery(id+"F31.wireOp",EDGE,"E146")}),1.0]])]});
            var Q1;
            Q1=makeQuery(id+"F31.imprint","IMPRINT",FACE,{"disambiguationData":[TD([[makeQuery(id+"F31.imprint","IMPRINT",EDGE,{"derivedFrom":sQuery(id+"F31.wireOp",EDGE,"E158.MirrorCS")}),-1.0]])]});
            var Q2;
            Q2=makeQuery(id+"F31.imprint","IMPRINT",FACE,{"disambiguationData":[TD([[makeQuery(id+"F31.imprint","IMPRINT",EDGE,{"derivedFrom":sQuery(id+"F31.wireOp",EDGE,"E164.MirrorCS")}),1.0]])]});
            var Q3;
            Q3=makeQuery(id+"F31.imprint","IMPRINT",FACE,{"disambiguationData":[TD([[makeQuery(id+"F31.imprint","IMPRINT",EDGE,{"derivedFrom":sQuery(id+"F31.wireOp",EDGE,"E152.MirrorCS")}),-1.0]])]});
            extrude(context, id + "F32", {"entities" : qUnion([Q0, Q1, Q2, Q3]), "operationType" : NewBodyOperationType.ADD, "depth" : 558.8 * mm, "offsetDistance" : 25.4 * mm});
        }
        {
            var Q0;
            Q0=makeQuery(id+"F32.opExtrude","SWEPT_FACE",FACE,{"disambiguationData":[OSD([sQuery(id+"F31.wireOp",EDGE,"E148")])]});
            var sketch = newSketch(context, id + "F33", { "sketchPlane" : qUnion([Q0])});
            skLineSegment(sketch, "E169", {"start": v(1125.29, 1854.2) * mm, "end": v(769.69, 1854.2) * mm});
            skLineSegment(sketch, "E170", {"start": v(769.69, 1854.2) * mm, "end": v(1125.29, 1854.2) * mm});
            skLineSegment(sketch, "E171", {"start": v(1023.69, 1854.2) * mm, "end": v(1379.29, 1854.2) * mm});
            skPoint(sketch, "E171.endSnap0", {"position": v(1074.49, 1854.2) * mm});
            skLineSegment(sketch, "E172", {"start": v(1379.29, 1854.2) * mm, "end": v(1379.29, 1447.8) * mm});
            skLineSegment(sketch, "E173", {"start": v(1379.29, 1447.8) * mm, "end": v(769.69, 1447.8) * mm});
            skLineSegment(sketch, "E174", {"start": v(769.69, 1447.8) * mm, "end": v(769.69, 1854.2) * mm});
            skLineSegment(sketch, "E175.0.0", {"start": v(0, 0) * mm, "end": v(11557, 0) * mm});
            skLineSegment(sketch, "E175.0.1", {"start": v(11557, 0) * mm, "end": v(11557, 3352.8) * mm});
            skLineSegment(sketch, "E175.0.2", {"start": v(11557, 3352.8) * mm, "end": v(0, 3352.8) * mm});
            skLineSegment(sketch, "E175.0.3", {"start": v(0, 3352.8) * mm, "end": v(0, 0) * mm});
            skLineSegment(sketch, "E176.0", {"start": v(4151.17, 1219.2) * mm, "end": v(3135.17, 1219.2) * mm});
            skPoint(sketch, "E177.0", {"position": v(3643.17, 1854.2) * mm});
            skLineSegment(sketch, "E178.0", {"start": v(566.49, 1219.2) * mm, "end": v(1582.49, 1219.2) * mm});
            skLineSegment(sketch, "E179.MirrorCS", {"start": v(3338.37, 1854.2) * mm, "end": v(3338.37, 1447.8) * mm});
            skLineSegment(sketch, "E180.MirrorCS", {"start": v(3338.37, 1447.8) * mm, "end": v(3947.97, 1447.8) * mm});
            skLineSegment(sketch, "E181.MirrorCS", {"start": v(3947.97, 1447.8) * mm, "end": v(3947.97, 1854.2) * mm});
            skLineSegment(sketch, "E182.MirrorCS", {"start": v(3947.97, 1854.2) * mm, "end": v(3592.37, 1854.2) * mm});
            skLineSegment(sketch, "E183.MirrorCS", {"start": v(3693.97, 1854.2) * mm, "end": v(3338.37, 1854.2) * mm});
            skLineSegment(sketch, "E184.0", {"start": v(7405.83, 1219.2) * mm, "end": v(8421.83, 1219.2) * mm});
            skLineSegment(sketch, "E185.MirrorCS", {"start": v(8218.63, 1447.8) * mm, "end": v(7609.03, 1447.8) * mm});
            skLineSegment(sketch, "E186.MirrorCS", {"start": v(7863.03, 1854.2) * mm, "end": v(8218.63, 1854.2) * mm});
            skLineSegment(sketch, "E187.MirrorCS", {"start": v(7609.03, 1854.2) * mm, "end": v(7964.63, 1854.2) * mm});
            skLineSegment(sketch, "E188.MirrorCS", {"start": v(7609.03, 1447.8) * mm, "end": v(7609.03, 1854.2) * mm});
            skLineSegment(sketch, "E189.MirrorCS", {"start": v(8218.63, 1854.2) * mm, "end": v(8218.63, 1447.8) * mm});
            skLineSegment(sketch, "E190.MirrorCS", {"start": v(10177.71, 1854.2) * mm, "end": v(10177.71, 1447.8) * mm});
            skLineSegment(sketch, "E191.MirrorCS", {"start": v(10177.71, 1447.8) * mm, "end": v(10787.31, 1447.8) * mm});
            skLineSegment(sketch, "E192.MirrorCS", {"start": v(10787.31, 1447.8) * mm, "end": v(10787.31, 1854.2) * mm});
            skLineSegment(sketch, "E193.MirrorCS", {"start": v(10787.31, 1854.2) * mm, "end": v(10431.71, 1854.2) * mm});
            skLineSegment(sketch, "E194.MirrorCS", {"start": v(10533.31, 1854.2) * mm, "end": v(10177.71, 1854.2) * mm});
            skSolve(sketch);
        }
        {
            var Q0;
            {var subQ0=sQuery(id+"F33.wireOp",EDGE,"E170");Q0=makeQuery(id+"F33.imprint","IMPRINT",FACE,{"disambiguationData":[TD([[makeQuery(id+"F33.imprint","IMPRINT",EDGE,{"derivedFrom":subQ0}),-1.0]])]});}
            var Q1;
            {var subQ1=sQuery(id+"F31.wireOp",EDGE,"E148");var subQ4=makeQuery(id+"F32.opExtrude","SWEPT_EDGE",EDGE,{"disambiguationData":[OSD([subQ1,sQuery(id+"F31.wireOp",EDGE,"E149")])]});var subQ6=sQuery(id+"F33.wireOp",EDGE,"E173");var subQ8=makeQuery(id+"F33.imprint","INTERSECT",VERTEX,{"derivedFrom":[subQ4,subQ6]});Q1=makeQuery(id+"F33.imprint","IMPRINT",FACE,{"disambiguationData":[TD([[makeQuery(id+"F33.imprint","IMPRINT",EDGE,{"disambiguationData":[TD([[subQ8,-1.0]])],"derivedFrom":subQ6}),-1.0]])]});}
            var Q2;
            {var subQ3=sQuery(id+"F33.wireOp",EDGE,"E172");Q2=makeQuery(id+"F33.imprint","IMPRINT",FACE,{"disambiguationData":[TD([[makeQuery(id+"F33.imprint","IMPRINT",EDGE,{"derivedFrom":subQ3}),-1.0]])]});}
            var Q3;
            {var subQ1=sQuery(id+"F33.wireOp",EDGE,"E179.MirrorCS");Q3=makeQuery(id+"F33.imprint","IMPRINT",FACE,{"disambiguationData":[TD([[makeQuery(id+"F33.imprint","IMPRINT",EDGE,{"derivedFrom":subQ1}),1.0]])]});}
            var Q4;
            Q4=makeQuery(id+"F33.imprint","IMPRINT",FACE,{"disambiguationData":[TD([[makeQuery(id+"F33.imprint","IMPRINT",EDGE,{"derivedFrom":sQuery(id+"F33.wireOp",EDGE,"E185.MirrorCS")}),-1.0]])]});
            var Q5;
            {var subQ1=sQuery(id+"F33.wireOp",EDGE,"E190.MirrorCS");Q5=makeQuery(id+"F33.imprint","IMPRINT",FACE,{"disambiguationData":[TD([[makeQuery(id+"F33.imprint","IMPRINT",EDGE,{"derivedFrom":subQ1}),1.0]])]});}
            extrude(context, id + "F34", {"entities" : qUnion([Q0, Q1, Q2, Q3, Q4, Q5]), "operationType" : NewBodyOperationType.ADD, "depth" : 50.8 * mm, "offsetDistance" : 25.4 * mm});
        }
        {
            var Q0;
            Q0=makeQuery(id+"F1.opExtrude","SWEPT_FACE",FACE,{"disambiguationData":[OSD([sQuery(id+"F0.wireOp",EDGE,"E32")])]});
            var sketch = newSketch(context, id + "F35", { "sketchPlane" : qUnion([Q0])});
            skLineSegment(sketch, "E195", {"start": v(0, 3352.8) * mm, "end": v(11557, 3352.8) * mm});
            skLineSegment(sketch, "E196", {"start": v(4635.5, 2844.8) * mm, "end": v(4635.5, 1574.8) * mm});
            skLineSegment(sketch, "E197", {"start": v(4635.5, 1574.8) * mm, "end": v(6921.5, 1574.8) * mm});
            skLineSegment(sketch, "E198", {"start": v(6921.5, 1574.8) * mm, "end": v(6921.5, 2844.8) * mm});
            skLineSegment(sketch, "E199", {"start": v(4635.5, 2844.8) * mm, "end": v(4635.5, 3098.8) * mm});
            skLineSegment(sketch, "E200", {"start": v(4635.5, 3098.8) * mm, "end": v(6921.5, 3098.8) * mm});
            skLineSegment(sketch, "E201", {"start": v(6921.5, 3098.8) * mm, "end": v(6921.5, 2844.8) * mm});
            skSolve(sketch);
        }
        {
            var Q0;
            Q0 = qSketchRegion(id + "F35", true);
            extrude(context, id + "F36", {"entities" : qUnion([Q0]), "operationType" : NewBodyOperationType.ADD, "depth" : 127 * mm, "offsetDistance" : 25.4 * mm});
        }
        {
            var Q0;
            Q0=makeQuery(id+"F14.opExtrude","CAP_FACE",FACE,{"disambiguationData":[OSD([sQuery(id+"F13.wireOp",EDGE,"E76.bottom"),sQuery(id+"F13.wireOp",EDGE,"E76.top"),sQuery(id+"F13.wireOp",EDGE,"E76.left"),sQuery(id+"F13.wireOp",EDGE,"E76.right")])],"isStart":false});
            var sketch = newSketch(context, id + "F37", { "sketchPlane" : qUnion([Q0])});
            skLineSegment(sketch, "E202", {"start": v(0, -3769.1) * mm, "end": v(7620, -3769.1) * mm});
            skLineSegment(sketch, "E203", {"start": v(3200.4, -4259.45) * mm, "end": v(3200.4, -4056.25) * mm});
            skLineSegment(sketch, "E204", {"start": v(3200.4, -4056.25) * mm, "end": v(4419.6, -4056.25) * mm});
            skLineSegment(sketch, "E205", {"start": v(4419.6, -4056.25) * mm, "end": v(4419.6, -4462.65) * mm});
            skLineSegment(sketch, "E206", {"start": v(4419.6, -4462.65) * mm, "end": v(3200.4, -4462.65) * mm});
            skLineSegment(sketch, "E207", {"start": v(3200.4, -4462.65) * mm, "end": v(3200.4, -4259.45) * mm});
            skLineSegment(sketch, "E208", {"start": v(3810, -4259.45) * mm, "end": v(3810, -4157.85) * mm});
            skPoint(sketch, "E208.startSnap0", {"position": v(3810, -4056.25) * mm});
            skLineSegment(sketch, "E209", {"start": v(3810, -4157.85) * mm, "end": v(3556, -4157.85) * mm});
            skLineSegment(sketch, "E210", {"start": v(3556, -4157.85) * mm, "end": v(3556, -4361.05) * mm});
            skLineSegment(sketch, "E211", {"start": v(3556, -4361.05) * mm, "end": v(4064, -4361.05) * mm});
            skLineSegment(sketch, "E212", {"start": v(4064, -4361.05) * mm, "end": v(4064, -4157.85) * mm});
            skLineSegment(sketch, "E213", {"start": v(4064, -4157.85) * mm, "end": v(3810, -4157.85) * mm});
            skSolve(sketch);
        }
        {
            var Q0;
            Q0 = qSketchRegion(id + "F37", true);
            extrude(context, id + "F38", {"entities" : qUnion([Q0]), "operationType" : NewBodyOperationType.ADD, "depth" : 203.2 * mm, "offsetDistance" : 25.4 * mm});
        }
        {
            var Q0;
            Q0=makeQuery(id+"F38.boolean.opBoolean","SPLIT",FACE,{"disambiguationData":[TD([makeQuery(id+"F38.opExtrude","SWEPT_FACE",FACE,{"disambiguationData":[OSD([sQuery(id+"F37.wireOp",EDGE,"E210")])]})])],"derivedFrom":makeQuery(id+"F14.opExtrude","CAP_FACE",FACE,{"disambiguationData":[OSD([sQuery(id+"F13.wireOp",EDGE,"E76.bottom"),sQuery(id+"F13.wireOp",EDGE,"E76.top"),sQuery(id+"F13.wireOp",EDGE,"E76.left"),sQuery(id+"F13.wireOp",EDGE,"E76.right")])],"isStart":false})});
            extrude(context, id + "F39", {"entities" : qUnion([Q0]), "operationType" : NewBodyOperationType.ADD, "depth" : 304.8 * mm, "offsetDistance" : 25.4 * mm});
        }
        {
            var Q0;
            Q0=makeQuery(id+"F39.opExtrude","CAP_FACE",FACE,{"disambiguationData":[OSD([sQuery(id+"F13.wireOp",EDGE,"E76.bottom"),sQuery(id+"F13.wireOp",EDGE,"E76.top"),sQuery(id+"F13.wireOp",EDGE,"E76.left"),sQuery(id+"F13.wireOp",EDGE,"E76.right")])],"isStart":false});
            var sketch = newSketch(context, id + "F40", { "sketchPlane" : qUnion([Q0])});
            skPoint(sketch, "E214.endSnap0", {"position": v(4064, -4259.45) * mm});
            skPoint(sketch, "E214.endSnap1", {"position": v(3810, -4361.05) * mm});
            skLineSegment(sketch, "E215", {"start": v(3810, -4259.45) * mm, "end": v(3810, -4310.25) * mm});
            skLineSegment(sketch, "E216", {"start": v(3810, -4310.25) * mm, "end": v(3860.8, -4310.25) * mm});
            skLineSegment(sketch, "E217", {"start": v(3860.8, -4310.25) * mm, "end": v(3860.8, -4208.65) * mm});
            skLineSegment(sketch, "E218", {"start": v(3860.8, -4208.65) * mm, "end": v(3759.2, -4208.65) * mm});
            skLineSegment(sketch, "E219", {"start": v(3759.2, -4208.65) * mm, "end": v(3759.2, -4310.25) * mm});
            skLineSegment(sketch, "E220", {"start": v(3759.2, -4310.25) * mm, "end": v(3810, -4310.25) * mm});
            skSolve(sketch);
        }
        {
            var Q0;
            Q0 = qSketchRegion(id + "F40", true);
            extrude(context, id + "F41", {"entities" : qUnion([Q0]), "operationType" : NewBodyOperationType.ADD, "depth" : 558.8 * mm, "offsetDistance" : 25.4 * mm});
        }
        {
            var Q0;
            Q0=makeQuery(id+"F41.opExtrude","SWEPT_FACE",FACE,{"disambiguationData":[OSD([sQuery(id+"F40.wireOp",EDGE,"E218")])]});
            var sketch = newSketch(context, id + "F42", { "sketchPlane" : qUnion([Q0])});
            skLineSegment(sketch, "E221", {"start": v(-3810, 1879.6) * mm, "end": v(-4165.6, 1879.6) * mm});
            skLineSegment(sketch, "E222", {"start": v(-4165.6, 1879.6) * mm, "end": v(-4165.6, 1473.2) * mm});
            skLineSegment(sketch, "E223", {"start": v(-4165.6, 1473.2) * mm, "end": v(-3533.27, 1473.2) * mm});
            skLineSegment(sketch, "E224", {"start": v(-3810, 1879.6) * mm, "end": v(-3454.4, 1879.6) * mm});
            skLineSegment(sketch, "E225", {"start": v(-3454.4, 1879.6) * mm, "end": v(-3454.4, 1473.2) * mm});
            skLineSegment(sketch, "E226", {"start": v(-3454.4, 1473.2) * mm, "end": v(-3533.27, 1473.2) * mm});
            skSolve(sketch);
        }
        {
            var Q0;
            Q0 = qSketchRegion(id + "F42", true);
            extrude(context, id + "F43", {"entities" : qUnion([Q0]), "operationType" : NewBodyOperationType.ADD, "depth" : 50.8 * mm, "offsetDistance" : 25.4 * mm});
        }
        {
            var Q0;
            {var subQ0=sQuery(id+"F13.wireOp",EDGE,"E76.left");var subQ1=sQuery(id+"F13.wireOp",EDGE,"E76.top");var subQ2=sQuery(id+"F13.wireOp",EDGE,"E76.right");var subQ3=sQuery(id+"F13.wireOp",EDGE,"E76.bottom");Q0=makeQuery(id+"F38.boolean.opBoolean","SPLIT",FACE,{"disambiguationData":[TD([makeQuery(id+"F14.opExtrude","SWEPT_FACE",FACE,{"disambiguationData":[OSD([subQ3])]})])],"derivedFrom":makeQuery(id+"F14.opExtrude","CAP_FACE",FACE,{"disambiguationData":[OSD([subQ3,subQ1,subQ0,subQ2])],"isStart":false})});}
            var sketch = newSketch(context, id + "F44", { "sketchPlane" : qUnion([Q0])});
            skLineSegment(sketch, "E227", {"start": v(0, -4749.8) * mm, "end": v(0, -3769.1) * mm});
            skLineSegment(sketch, "E228", {"start": v(190.5, -4023.1) * mm, "end": v(190.5, -4632.7) * mm});
            skLineSegment(sketch, "E229", {"start": v(190.5, -4632.7) * mm, "end": v(1409.7, -4632.7) * mm});
            skLineSegment(sketch, "E230", {"start": v(1409.7, -4632.7) * mm, "end": v(1409.7, -3870.7) * mm});
            skLineSegment(sketch, "E231", {"start": v(1409.7, -3870.7) * mm, "end": v(190.5, -3870.7) * mm});
            skLineSegment(sketch, "E232", {"start": v(190.5, -3870.7) * mm, "end": v(190.5, -4023.1) * mm});
            skLineSegment(sketch, "E233.MirrorCS", {"start": v(1790.7, -4632.7) * mm, "end": v(1790.7, -3870.7) * mm});
            skLineSegment(sketch, "E234.MirrorCS", {"start": v(3009.9, -4023.1) * mm, "end": v(3009.9, -4632.7) * mm});
            skLineSegment(sketch, "E235.MirrorCS", {"start": v(3009.9, -3870.7) * mm, "end": v(3009.9, -4023.1) * mm});
            skLineSegment(sketch, "E236.MirrorCS", {"start": v(1790.7, -3870.7) * mm, "end": v(3009.9, -3870.7) * mm});
            skLineSegment(sketch, "E237.MirrorCS", {"start": v(3009.9, -4632.7) * mm, "end": v(1790.7, -4632.7) * mm});
            skLineSegment(sketch, "E238.MirrorCS", {"start": v(4610.1, -4023.1) * mm, "end": v(4610.1, -4632.7) * mm});
            skLineSegment(sketch, "E239.MirrorCS", {"start": v(4610.1, -3870.7) * mm, "end": v(4610.1, -4023.1) * mm});
            skLineSegment(sketch, "E240.MirrorCS", {"start": v(5829.3, -3870.7) * mm, "end": v(4610.1, -3870.7) * mm});
            skLineSegment(sketch, "E241.MirrorCS", {"start": v(5829.3, -4632.7) * mm, "end": v(5829.3, -3870.7) * mm});
            skLineSegment(sketch, "E242.MirrorCS", {"start": v(4610.1, -4632.7) * mm, "end": v(5829.3, -4632.7) * mm});
            skLineSegment(sketch, "E243.MirrorCS", {"start": v(7429.5, -4632.7) * mm, "end": v(6210.3, -4632.7) * mm});
            skLineSegment(sketch, "E244.MirrorCS", {"start": v(7429.5, -4023.1) * mm, "end": v(7429.5, -4632.7) * mm});
            skLineSegment(sketch, "E245.MirrorCS", {"start": v(7429.5, -3870.7) * mm, "end": v(7429.5, -4023.1) * mm});
            skLineSegment(sketch, "E246.MirrorCS", {"start": v(6210.3, -3870.7) * mm, "end": v(7429.5, -3870.7) * mm});
            skLineSegment(sketch, "E247.MirrorCS", {"start": v(6210.3, -4632.7) * mm, "end": v(6210.3, -3870.7) * mm});
            skSolve(sketch);
        }
        {
            var Q0;
            Q0 = qSketchRegion(id + "F44", true);
            extrude(context, id + "F45", {"entities" : qUnion([Q0]), "operationType" : NewBodyOperationType.ADD, "depth" : 889 * mm, "offsetDistance" : 25.4 * mm});
        }
        {
            var Q0;
            Q0=makeQuery(id+"F45.opExtrude","SWEPT_FACE",FACE,{"disambiguationData":[OSD([sQuery(id+"F44.wireOp",EDGE,"E246.MirrorCS")])]});
            var sketch = newSketch(context, id + "F46", { "sketchPlane" : qUnion([Q0])});
            skLineSegment(sketch, "E248", {"start": v(-7277.1, 1168.4) * mm, "end": v(-6362.7, 1168.4) * mm});
            skLineSegment(sketch, "E249", {"start": v(-6362.7, 1168.4) * mm, "end": v(-6362.7, 1752.6) * mm});
            skLineSegment(sketch, "E250", {"start": v(-6362.7, 1752.6) * mm, "end": v(-7277.1, 1752.6) * mm});
            skLineSegment(sketch, "E251", {"start": v(-7277.1, 1168.4) * mm, "end": v(-7277.1, 1752.6) * mm});
            skLineSegment(sketch, "E252.0.0", {"start": v(-5829.3, 1016) * mm, "end": v(-4610.1, 1016) * mm});
            skLineSegment(sketch, "E252.0.1", {"start": v(-4610.1, 1016) * mm, "end": v(-4610.1, 1905) * mm});
            skLineSegment(sketch, "E252.0.2", {"start": v(-4610.1, 1905) * mm, "end": v(-5829.3, 1905) * mm});
            skLineSegment(sketch, "E252.0.3", {"start": v(-5829.3, 1905) * mm, "end": v(-5829.3, 1016) * mm});
            skLineSegment(sketch, "E253", {"start": v(-7429.5, 1016) * mm, "end": v(-4610.1, 1016) * mm});
            skLineSegment(sketch, "E254", {"start": v(-6019.8, 1016) * mm, "end": v(-6019.8, 1211.11) * mm});
            skLineSegment(sketch, "E255.MirrorCS", {"start": v(-5676.9, 1168.4) * mm, "end": v(-5676.9, 1752.6) * mm});
            skLineSegment(sketch, "E256.MirrorCS", {"start": v(-5676.9, 1752.6) * mm, "end": v(-4762.5, 1752.6) * mm});
            skLineSegment(sketch, "E257.MirrorCS", {"start": v(-4762.5, 1168.4) * mm, "end": v(-4762.5, 1752.6) * mm});
            skLineSegment(sketch, "E258.MirrorCS", {"start": v(-4762.5, 1168.4) * mm, "end": v(-5676.9, 1168.4) * mm});
            skLineSegment(sketch, "E259.0.0", {"start": v(-3009.9, 1016) * mm, "end": v(-1790.7, 1016) * mm});
            skLineSegment(sketch, "E259.0.1", {"start": v(-1790.7, 1016) * mm, "end": v(-1790.7, 1905) * mm});
            skLineSegment(sketch, "E259.0.2", {"start": v(-1790.7, 1905) * mm, "end": v(-3009.9, 1905) * mm});
            skLineSegment(sketch, "E259.0.3", {"start": v(-3009.9, 1905) * mm, "end": v(-3009.9, 1016) * mm});
            skLineSegment(sketch, "E260", {"start": v(-4610.1, 1016) * mm, "end": v(-3009.9, 1016) * mm});
            skLineSegment(sketch, "E261", {"start": v(-3810, 1016) * mm, "end": v(-3810, 1168.4) * mm});
            skLineSegment(sketch, "E262.MirrorCS", {"start": v(-2857.5, 1168.4) * mm, "end": v(-2857.5, 1752.6) * mm});
            skLineSegment(sketch, "E263.MirrorCS", {"start": v(-1943.1, 1752.6) * mm, "end": v(-2857.5, 1752.6) * mm});
            skLineSegment(sketch, "E264.MirrorCS", {"start": v(-1943.1, 1168.4) * mm, "end": v(-1943.1, 1752.6) * mm});
            skLineSegment(sketch, "E265.MirrorCS", {"start": v(-2857.5, 1168.4) * mm, "end": v(-1943.1, 1168.4) * mm});
            skLineSegment(sketch, "E266.MirrorCS", {"start": v(-1257.3, 1168.4) * mm, "end": v(-1257.3, 1752.6) * mm});
            skLineSegment(sketch, "E267.MirrorCS", {"start": v(-1257.3, 1752.6) * mm, "end": v(-342.9, 1752.6) * mm});
            skLineSegment(sketch, "E268.MirrorCS", {"start": v(-342.9, 1168.4) * mm, "end": v(-342.9, 1752.6) * mm});
            skLineSegment(sketch, "E269.MirrorCS", {"start": v(-342.9, 1168.4) * mm, "end": v(-1257.3, 1168.4) * mm});
            skSolve(sketch);
        }
        {
            var Q0;
            Q0=makeQuery(id+"F46.imprint","IMPRINT",FACE,{"disambiguationData":[TD([[makeQuery(id+"F46.imprint","IMPRINT",EDGE,{"derivedFrom":sQuery(id+"F46.wireOp",EDGE,"E248")}),1.0]])]});
            var Q1;
            Q1=makeQuery(id+"F46.imprint","IMPRINT",FACE,{"disambiguationData":[TD([[makeQuery(id+"F46.imprint","IMPRINT",EDGE,{"derivedFrom":sQuery(id+"F46.wireOp",EDGE,"E255.MirrorCS")}),-1.0]])]});
            var Q2;
            Q2=makeQuery(id+"F46.imprint","IMPRINT",FACE,{"disambiguationData":[TD([[makeQuery(id+"F46.imprint","IMPRINT",EDGE,{"derivedFrom":sQuery(id+"F46.wireOp",EDGE,"E262.MirrorCS")}),-1.0]])]});
            var Q3;
            Q3=makeQuery(id+"F46.imprint","IMPRINT",FACE,{"disambiguationData":[TD([[makeQuery(id+"F46.imprint","IMPRINT",EDGE,{"derivedFrom":sQuery(id+"F46.wireOp",EDGE,"E266.MirrorCS")}),-1.0]])]});
            extrude(context, id + "F47", {"entities" : qUnion([Q0, Q1, Q2, Q3]), "operationType" : NewBodyOperationType.REMOVE, "oppositeDirection" : true, "depth" : 609.6 * mm, "offsetDistance" : 25.4 * mm});
        }
        {
            var Q0;
            Q0=makeQuery(id+"F47.boolean.opBoolean","COPY",FACE,{"derivedFrom":makeQuery(id+"F47.opExtrude","SWEPT_FACE",FACE,{"disambiguationData":[OSD([sQuery(id+"F46.wireOp",EDGE,"E248")])]})});
            var sketch = newSketch(context, id + "F48", { "sketchPlane" : qUnion([Q0])});
            skLineSegment(sketch, "E270.bottom", {"start": v(6581.7, -4001.27) * mm, "end": v(7058.1, -4001.27) * mm});
            skLineSegment(sketch, "E270.top", {"start": v(6581.7, -4349.74) * mm, "end": v(7058.1, -4349.74) * mm});
            skLineSegment(sketch, "E270.left", {"start": v(6581.7, -4001.27) * mm, "end": v(6581.7, -4349.74) * mm});
            skLineSegment(sketch, "E270.right", {"start": v(7058.1, -4001.27) * mm, "end": v(7058.1, -4349.74) * mm});
            skPoint(sketch, "E270.middle", {"position": v(6819.9, -4175.5) * mm});
            skPoint(sketch, "E270.middle.positionSnap0", {"position": v(6819.9, -3870.7) * mm});
            skPoint(sketch, "E270.middle.positionSnap1", {"position": v(7277.1, -4175.5) * mm});
            skPoint(sketch, "E270.centerSnap0", {"position": v(6819.9, -3870.7) * mm});
            skPoint(sketch, "E270.centerSnap1", {"position": v(7277.1, -4175.5) * mm});
            skLineSegment(sketch, "E271.0.1", {"start": v(4762.5, -3870.7) * mm, "end": v(4762.5, -4480.3) * mm});
            skLineSegment(sketch, "E271.0.2", {"start": v(4762.5, -4480.3) * mm, "end": v(5676.9, -4480.3) * mm});
            skLineSegment(sketch, "E271.0.3", {"start": v(5676.9, -4480.3) * mm, "end": v(5676.9, -3870.7) * mm});
            skLineSegment(sketch, "E272.0.0", {"start": v(2857.5, -3870.7) * mm, "end": v(1943.1, -3870.7) * mm});
            skLineSegment(sketch, "E272.0.1", {"start": v(1943.1, -3870.7) * mm, "end": v(1943.1, -4480.3) * mm});
            skLineSegment(sketch, "E272.0.2", {"start": v(1943.1, -4480.3) * mm, "end": v(2857.5, -4480.3) * mm});
            skLineSegment(sketch, "E272.0.3", {"start": v(2857.5, -4480.3) * mm, "end": v(2857.5, -3870.7) * mm});
            skLineSegment(sketch, "E273.0.0", {"start": v(1257.3, -3870.7) * mm, "end": v(342.9, -3870.7) * mm});
            skLineSegment(sketch, "E273.0.1", {"start": v(342.9, -3870.7) * mm, "end": v(342.9, -4480.3) * mm});
            skLineSegment(sketch, "E273.0.2", {"start": v(342.9, -4480.3) * mm, "end": v(1257.3, -4480.3) * mm});
            skLineSegment(sketch, "E273.0.3", {"start": v(1257.3, -4480.3) * mm, "end": v(1257.3, -3870.7) * mm});
            skLineSegment(sketch, "E274.MirrorCS", {"start": v(5457.9, -4001.27) * mm, "end": v(4981.5, -4001.27) * mm});
            skLineSegment(sketch, "E275.MirrorCS", {"start": v(4981.5, -4001.27) * mm, "end": v(4981.5, -4349.74) * mm});
            skLineSegment(sketch, "E276.MirrorCS", {"start": v(5457.9, -4349.74) * mm, "end": v(4981.5, -4349.74) * mm});
            skLineSegment(sketch, "E277.MirrorCS", {"start": v(5457.9, -4001.27) * mm, "end": v(5457.9, -4349.74) * mm});
            skLineSegment(sketch, "E278.MirrorCS", {"start": v(2162.1, -4001.27) * mm, "end": v(2638.5, -4001.27) * mm});
            skLineSegment(sketch, "E279.MirrorCS", {"start": v(2162.1, -4001.27) * mm, "end": v(2162.1, -4349.74) * mm});
            skLineSegment(sketch, "E280.MirrorCS", {"start": v(2162.1, -4349.74) * mm, "end": v(2638.5, -4349.74) * mm});
            skLineSegment(sketch, "E281.MirrorCS", {"start": v(2638.5, -4001.27) * mm, "end": v(2638.5, -4349.74) * mm});
            skLineSegment(sketch, "E282.MirrorCS", {"start": v(1038.3, -4001.27) * mm, "end": v(561.9, -4001.27) * mm});
            skLineSegment(sketch, "E283.MirrorCS", {"start": v(561.9, -4001.27) * mm, "end": v(561.9, -4349.74) * mm});
            skLineSegment(sketch, "E284.MirrorCS", {"start": v(1038.3, -4349.74) * mm, "end": v(561.9, -4349.74) * mm});
            skLineSegment(sketch, "E285.MirrorCS", {"start": v(1038.3, -4001.27) * mm, "end": v(1038.3, -4349.74) * mm});
            skSolve(sketch);
        }
        {
            var Q0;
            Q0=makeQuery(id+"F48.imprint","IMPRINT",FACE,{"disambiguationData":[TD([[makeQuery(id+"F48.imprint","IMPRINT",EDGE,{"derivedFrom":sQuery(id+"F48.wireOp",EDGE,"E270.bottom")}),-1.0]])]});
            var Q1;
            Q1=makeQuery(id+"F48.imprint","IMPRINT",FACE,{"disambiguationData":[TD([[makeQuery(id+"F48.imprint","IMPRINT",EDGE,{"derivedFrom":sQuery(id+"F48.wireOp",EDGE,"E274.MirrorCS")}),1.0]])]});
            var Q2;
            Q2=makeQuery(id+"F48.imprint","IMPRINT",FACE,{"disambiguationData":[TD([[makeQuery(id+"F48.imprint","IMPRINT",EDGE,{"derivedFrom":sQuery(id+"F48.wireOp",EDGE,"E278.MirrorCS")}),-1.0]])]});
            var Q3;
            Q3=makeQuery(id+"F48.imprint","IMPRINT",FACE,{"disambiguationData":[TD([[makeQuery(id+"F48.imprint","IMPRINT",EDGE,{"derivedFrom":sQuery(id+"F48.wireOp",EDGE,"E282.MirrorCS")}),1.0]])]});
            extrude(context, id + "F49", {"entities" : qUnion([Q0, Q1, Q2, Q3]), "operationType" : NewBodyOperationType.ADD, "depth" : 76.2 * mm, "offsetDistance" : 25.4 * mm});
        }
        {
            var Q0;
            Q0=makeQuery(id+"F8.opExtrude","CAP_FACE",FACE,{"disambiguationData":[OSD([sQuery(id+"F7.wireOp",EDGE,"E64")])],"isStart":false});
            var sketch = newSketch(context, id + "F50", { "sketchPlane" : qUnion([Q0])});
            skLineSegment(sketch, "E286.bottom", {"start": v(2784.46, 61.82) * mm, "end": v(2661.51, 61.82) * mm});
            skLineSegment(sketch, "E286.top", {"start": v(2784.46, -61.82) * mm, "end": v(2661.51, -61.82) * mm});
            skLineSegment(sketch, "E286.left", {"start": v(2784.46, 61.82) * mm, "end": v(2784.46, -61.82) * mm});
            skLineSegment(sketch, "E286.right", {"start": v(2661.51, 61.82) * mm, "end": v(2661.51, -61.82) * mm});
            skPoint(sketch, "E286.middle", {"position": v(2722.99, 0) * mm});
            skArc(sketch, "E287.0.0", {"start": v(8597.53, 1348.25) * mm, "mid": v(7662.51, 863.3) * mm, "end": v(6726.29, 1345.91) * mm});
            skArc(sketch, "E287.0.1", {"start": v(6726.29, 1345.91) * mm, "mid": v(6440.78, 1093.05) * mm, "end": v(6221.4, 781.08) * mm});
            skArc(sketch, "E287.0.2", {"start": v(6221.4, 781.08) * mm, "mid": v(6782.4, -46.3) * mm, "end": v(6311.2, -927.92) * mm});
            skArc(sketch, "E287.0.3", {"start": v(6311.2, -927.92) * mm, "mid": v(6523.82, -1179.39) * mm, "end": v(6782.4, -1383.3) * mm});
            skArc(sketch, "E287.0.4", {"start": v(6782.4, -1383.3) * mm, "mid": v(7680.2, -859.78) * mm, "end": v(8597.53, -1348.25) * mm});
            skArc(sketch, "E287.0.5", {"start": v(8597.53, -1348.25) * mm, "mid": v(8825.92, -1157.16) * mm, "end": v(9015.99, -927.92) * mm});
            skArc(sketch, "E287.0.6", {"start": v(9015.99, -927.92) * mm, "mid": v(8358, -36.49) * mm, "end": v(9105.79, 781.08) * mm});
            skArc(sketch, "E287.0.7", {"start": v(9105.79, 781.08) * mm, "mid": v(8885.04, 1094.57) * mm, "end": v(8597.53, 1348.25) * mm});
            skLineSegment(sketch, "E288.MirrorCS", {"start": v(7604.1, -61.82) * mm, "end": v(7727.04, -61.82) * mm});
            skLineSegment(sketch, "E289.MirrorCS", {"start": v(7727.04, 61.82) * mm, "end": v(7727.04, -61.82) * mm});
            skLineSegment(sketch, "E290.MirrorCS", {"start": v(7604.1, 61.82) * mm, "end": v(7727.04, 61.82) * mm});
            skLineSegment(sketch, "E291.MirrorCS", {"start": v(7604.1, 61.82) * mm, "end": v(7604.1, -61.82) * mm});
            skSolve(sketch);
        }
        {
            var Q0;
            Q0=makeQuery(id+"F50.imprint","IMPRINT",FACE,{"disambiguationData":[TD([[makeQuery(id+"F50.imprint","IMPRINT",EDGE,{"derivedFrom":sQuery(id+"F50.wireOp",EDGE,"E288.MirrorCS")}),1.0]])]});
            var Q1;
            Q1=makeQuery(id+"F50.imprint","IMPRINT",FACE,{"disambiguationData":[TD([[makeQuery(id+"F50.imprint","IMPRINT",EDGE,{"derivedFrom":sQuery(id+"F50.wireOp",EDGE,"E286.bottom")}),1.0]])]});
            extrude(context, id + "F51", {"entities" : qUnion([Q0, Q1]), "operationType" : NewBodyOperationType.ADD, "depth" : 2336.8 * mm, "offsetDistance" : 25.4 * mm});
        }
    });
